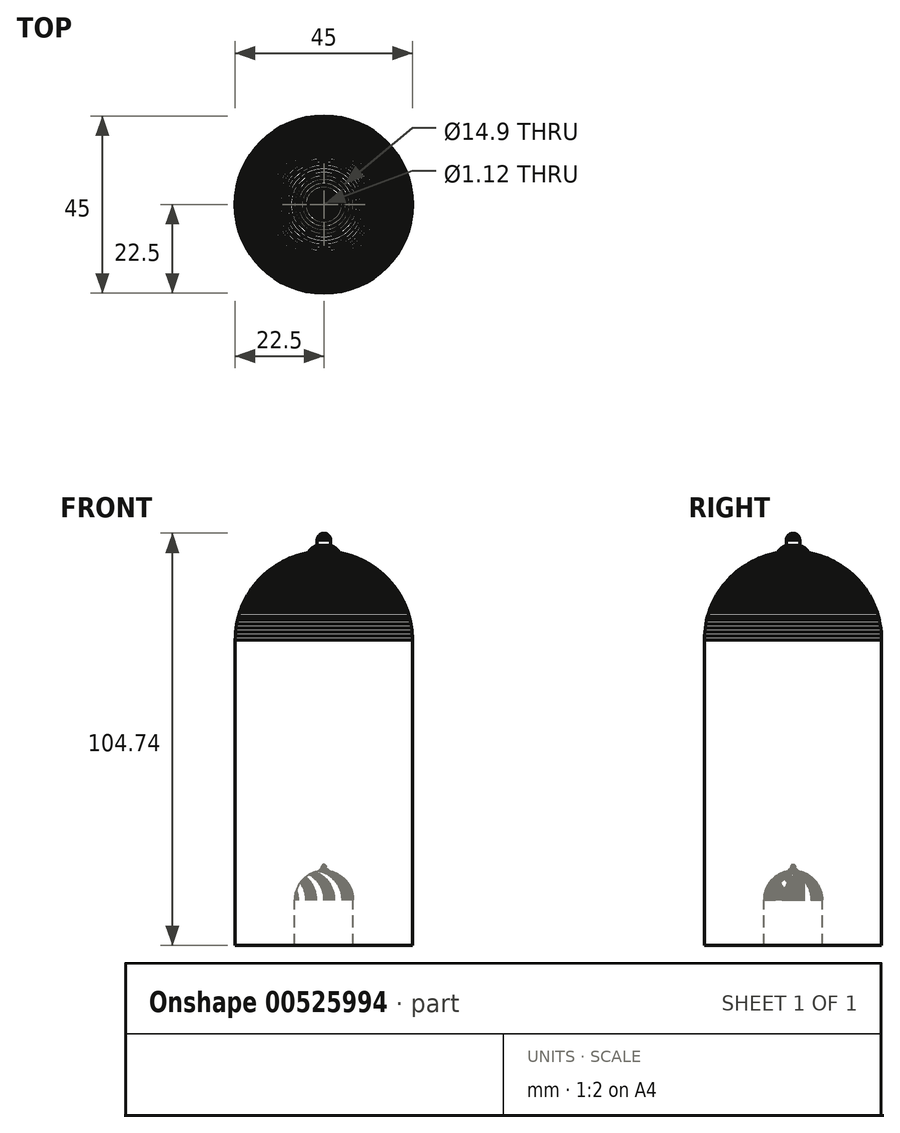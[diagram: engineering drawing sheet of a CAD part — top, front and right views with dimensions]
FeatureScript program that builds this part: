
annotation { "Feature Type Name" : "Feature", "Feature Type Description" : "" }
export const myFeature = defineFeature(function(context is Context, id is Id, definition is map)
    precondition{}
    {
        {
            var Q0;
            Q0=qCreatedBy(makeId("Front.planeOp"),FACE);
            var sketch = newSketch(context, id + "F0", { "sketchPlane" : qUnion([Q0])});
            skLineSegment(sketch, "E0", {"start": v(3.98, 47.42) * mm, "end": v(3.94, 47.5) * mm});
            skLineSegment(sketch, "E1", {"start": v(3.94, 47.5) * mm, "end": v(3.9, 47.57) * mm});
            skLineSegment(sketch, "E2", {"start": v(3.9, 47.57) * mm, "end": v(3.86, 47.65) * mm});
            skLineSegment(sketch, "E3", {"start": v(3.86, 47.65) * mm, "end": v(3.82, 47.72) * mm});
            skLineSegment(sketch, "E4", {"start": v(3.82, 47.72) * mm, "end": v(3.77, 47.8) * mm});
            skLineSegment(sketch, "E5", {"start": v(3.77, 47.8) * mm, "end": v(3.73, 47.87) * mm});
            skLineSegment(sketch, "E6", {"start": v(3.73, 47.87) * mm, "end": v(3.67, 47.94) * mm});
            skLineSegment(sketch, "E7", {"start": v(3.67, 47.94) * mm, "end": v(3.62, 48.01) * mm});
            skLineSegment(sketch, "E8", {"start": v(3.62, 48.01) * mm, "end": v(3.57, 48.08) * mm});
            skLineSegment(sketch, "E9", {"start": v(3.57, 48.08) * mm, "end": v(3.5, 48.15) * mm});
            skLineSegment(sketch, "E10", {"start": v(3.5, 48.15) * mm, "end": v(3.45, 48.22) * mm});
            skLineSegment(sketch, "E11", {"start": v(3.45, 48.22) * mm, "end": v(3.38, 48.28) * mm});
            skLineSegment(sketch, "E12", {"start": v(3.38, 48.28) * mm, "end": v(3.32, 48.34) * mm});
            skLineSegment(sketch, "E13", {"start": v(3.32, 48.34) * mm, "end": v(3.25, 48.4) * mm});
            skLineSegment(sketch, "E14", {"start": v(3.25, 48.4) * mm, "end": v(3.18, 48.47) * mm});
            skLineSegment(sketch, "E15", {"start": v(3.18, 48.47) * mm, "end": v(3.1, 48.53) * mm});
            skLineSegment(sketch, "E16", {"start": v(3.1, 48.53) * mm, "end": v(3.03, 48.59) * mm});
            skLineSegment(sketch, "E17", {"start": v(3.03, 48.59) * mm, "end": v(2.96, 48.65) * mm});
            skLineSegment(sketch, "E18", {"start": v(2.96, 48.65) * mm, "end": v(2.88, 48.7) * mm});
            skLineSegment(sketch, "E19", {"start": v(2.88, 48.7) * mm, "end": v(2.8, 48.76) * mm});
            skLineSegment(sketch, "E20", {"start": v(2.8, 48.76) * mm, "end": v(2.72, 48.8) * mm});
            skLineSegment(sketch, "E21", {"start": v(2.72, 48.8) * mm, "end": v(2.63, 48.86) * mm});
            skLineSegment(sketch, "E22", {"start": v(2.63, 48.86) * mm, "end": v(2.55, 48.9) * mm});
            skLineSegment(sketch, "E23", {"start": v(2.55, 48.9) * mm, "end": v(2.46, 48.96) * mm});
            skLineSegment(sketch, "E24", {"start": v(2.46, 48.96) * mm, "end": v(2.37, 49) * mm});
            skLineSegment(sketch, "E25", {"start": v(2.37, 49) * mm, "end": v(2.28, 49.05) * mm});
            skLineSegment(sketch, "E26", {"start": v(2.28, 49.05) * mm, "end": v(2.19, 49.1) * mm});
            skLineSegment(sketch, "E27", {"start": v(2.19, 49.1) * mm, "end": v(2.1, 49.13) * mm});
            skLineSegment(sketch, "E28", {"start": v(2.1, 49.13) * mm, "end": v(2, 49.17) * mm});
            skLineSegment(sketch, "E29", {"start": v(2, 49.17) * mm, "end": v(1.9, 49.2) * mm});
            skLineSegment(sketch, "E30", {"start": v(1.9, 49.2) * mm, "end": v(1.8, 49.25) * mm});
            skLineSegment(sketch, "E31", {"start": v(1.8, 49.25) * mm, "end": v(1.7, 49.28) * mm});
            skLineSegment(sketch, "E32", {"start": v(1.7, 49.28) * mm, "end": v(1.7, 49.32) * mm});
            skLineSegment(sketch, "E33", {"start": v(1.7, 49.32) * mm, "end": v(1.7, 49.37) * mm});
            skLineSegment(sketch, "E34", {"start": v(1.7, 49.37) * mm, "end": v(1.7, 49.4) * mm});
            skLineSegment(sketch, "E35", {"start": v(1.7, 49.4) * mm, "end": v(1.7, 49.45) * mm});
            skLineSegment(sketch, "E36", {"start": v(1.7, 49.45) * mm, "end": v(1.7, 49.5) * mm});
            skLineSegment(sketch, "E37", {"start": v(1.7, 49.5) * mm, "end": v(1.7, 49.54) * mm});
            skLineSegment(sketch, "E38", {"start": v(1.7, 49.54) * mm, "end": v(1.7, 49.58) * mm});
            skLineSegment(sketch, "E39", {"start": v(1.7, 49.58) * mm, "end": v(1.7, 49.63) * mm});
            skLineSegment(sketch, "E40", {"start": v(1.7, 49.63) * mm, "end": v(1.7, 49.67) * mm});
            skLineSegment(sketch, "E41", {"start": v(1.7, 49.67) * mm, "end": v(1.7, 49.71) * mm});
            skLineSegment(sketch, "E42", {"start": v(1.7, 49.71) * mm, "end": v(1.7, 49.76) * mm});
            skLineSegment(sketch, "E43", {"start": v(1.7, 49.76) * mm, "end": v(1.7, 49.8) * mm});
            skLineSegment(sketch, "E44", {"start": v(1.7, 49.8) * mm, "end": v(1.7, 49.84) * mm});
            skLineSegment(sketch, "E45", {"start": v(1.7, 49.84) * mm, "end": v(1.7, 49.89) * mm});
            skLineSegment(sketch, "E46", {"start": v(1.7, 49.89) * mm, "end": v(1.7, 49.93) * mm});
            skLineSegment(sketch, "E47", {"start": v(1.7, 49.93) * mm, "end": v(1.7, 49.97) * mm});
            skLineSegment(sketch, "E48", {"start": v(1.7, 49.97) * mm, "end": v(1.7, 50.02) * mm});
            skLineSegment(sketch, "E49", {"start": v(1.7, 50.02) * mm, "end": v(1.7, 50.06) * mm});
            skLineSegment(sketch, "E50", {"start": v(1.7, 50.06) * mm, "end": v(1.7, 50.1) * mm});
            skLineSegment(sketch, "E51", {"start": v(1.7, 50.1) * mm, "end": v(1.7, 50.15) * mm});
            skLineSegment(sketch, "E52", {"start": v(1.7, 50.15) * mm, "end": v(1.7, 50.2) * mm});
            skLineSegment(sketch, "E53", {"start": v(1.7, 50.2) * mm, "end": v(1.7, 50.23) * mm});
            skLineSegment(sketch, "E54", {"start": v(1.7, 50.23) * mm, "end": v(1.7, 50.28) * mm});
            skLineSegment(sketch, "E55", {"start": v(1.7, 50.28) * mm, "end": v(1.7, 50.32) * mm});
            skLineSegment(sketch, "E56", {"start": v(1.7, 50.32) * mm, "end": v(1.7, 50.36) * mm});
            skLineSegment(sketch, "E57", {"start": v(1.7, 50.36) * mm, "end": v(1.7, 50.4) * mm});
            skLineSegment(sketch, "E58", {"start": v(1.7, 50.4) * mm, "end": v(1.7, 50.45) * mm});
            skLineSegment(sketch, "E59", {"start": v(1.7, 50.45) * mm, "end": v(1.7, 50.5) * mm});
            skLineSegment(sketch, "E60", {"start": v(1.7, 50.5) * mm, "end": v(1.7, 50.54) * mm});
            skLineSegment(sketch, "E61", {"start": v(1.7, 50.54) * mm, "end": v(1.7, 50.58) * mm});
            skLineSegment(sketch, "E62", {"start": v(1.7, 50.58) * mm, "end": v(1.7, 50.63) * mm});
            skLineSegment(sketch, "E63", {"start": v(1.7, 50.63) * mm, "end": v(1.7, 50.67) * mm});
            skLineSegment(sketch, "E64", {"start": v(1.7, 50.67) * mm, "end": v(1.7, 50.76) * mm});
            skLineSegment(sketch, "E65", {"start": v(1.7, 50.76) * mm, "end": v(1.69, 50.84) * mm});
            skLineSegment(sketch, "E66", {"start": v(1.69, 50.84) * mm, "end": v(1.68, 50.93) * mm});
            skLineSegment(sketch, "E67", {"start": v(1.68, 50.93) * mm, "end": v(1.66, 51.01) * mm});
            skLineSegment(sketch, "E68", {"start": v(1.66, 51.01) * mm, "end": v(1.64, 51.1) * mm});
            skLineSegment(sketch, "E69", {"start": v(1.64, 51.1) * mm, "end": v(1.62, 51.17) * mm});
            skLineSegment(sketch, "E70", {"start": v(1.62, 51.17) * mm, "end": v(1.6, 51.25) * mm});
            skLineSegment(sketch, "E71", {"start": v(1.6, 51.25) * mm, "end": v(1.56, 51.33) * mm});
            skLineSegment(sketch, "E72", {"start": v(1.56, 51.33) * mm, "end": v(1.53, 51.4) * mm});
            skLineSegment(sketch, "E73", {"start": v(1.53, 51.4) * mm, "end": v(1.5, 51.48) * mm});
            skLineSegment(sketch, "E74", {"start": v(1.5, 51.48) * mm, "end": v(1.45, 51.55) * mm});
            skLineSegment(sketch, "E75", {"start": v(1.45, 51.55) * mm, "end": v(1.4, 51.62) * mm});
            skLineSegment(sketch, "E76", {"start": v(1.4, 51.62) * mm, "end": v(1.36, 51.68) * mm});
            skLineSegment(sketch, "E77", {"start": v(1.36, 51.68) * mm, "end": v(1.3, 51.75) * mm});
            skLineSegment(sketch, "E78", {"start": v(1.3, 51.75) * mm, "end": v(1.26, 51.8) * mm});
            skLineSegment(sketch, "E79", {"start": v(1.26, 51.8) * mm, "end": v(1.2, 51.87) * mm});
            skLineSegment(sketch, "E80", {"start": v(1.2, 51.87) * mm, "end": v(1.14, 51.92) * mm});
            skLineSegment(sketch, "E81", {"start": v(1.14, 51.92) * mm, "end": v(1.08, 51.98) * mm});
            skLineSegment(sketch, "E82", {"start": v(1.08, 51.98) * mm, "end": v(1.02, 52.03) * mm});
            skLineSegment(sketch, "E83", {"start": v(1.02, 52.03) * mm, "end": v(0.95, 52.08) * mm});
            skLineSegment(sketch, "E84", {"start": v(0.95, 52.08) * mm, "end": v(0.88, 52.12) * mm});
            skLineSegment(sketch, "E85", {"start": v(0.88, 52.12) * mm, "end": v(0.8, 52.16) * mm});
            skLineSegment(sketch, "E86", {"start": v(0.8, 52.16) * mm, "end": v(0.74, 52.2) * mm});
            skLineSegment(sketch, "E87", {"start": v(0.74, 52.2) * mm, "end": v(0.66, 52.23) * mm});
            skLineSegment(sketch, "E88", {"start": v(0.66, 52.23) * mm, "end": v(0.58, 52.26) * mm});
            skLineSegment(sketch, "E89", {"start": v(0.58, 52.26) * mm, "end": v(0.5, 52.29) * mm});
            skLineSegment(sketch, "E90", {"start": v(0.5, 52.29) * mm, "end": v(0.42, 52.31) * mm});
            skLineSegment(sketch, "E91", {"start": v(0.42, 52.31) * mm, "end": v(0.34, 52.33) * mm});
            skLineSegment(sketch, "E92", {"start": v(0.34, 52.33) * mm, "end": v(0.26, 52.35) * mm});
            skLineSegment(sketch, "E93", {"start": v(0.26, 52.35) * mm, "end": v(0.17, 52.36) * mm});
            skLineSegment(sketch, "E94", {"start": v(0.17, 52.36) * mm, "end": v(0.09, 52.36) * mm});
            skLineSegment(sketch, "E95", {"start": v(0, 52.37) * mm, "end": v(-0.09, 52.36) * mm});
            skLineSegment(sketch, "E96", {"start": v(-0.09, 52.36) * mm, "end": v(-0.17, 52.36) * mm});
            skLineSegment(sketch, "E97", {"start": v(-0.17, 52.36) * mm, "end": v(-0.26, 52.35) * mm});
            skLineSegment(sketch, "E98", {"start": v(-0.26, 52.35) * mm, "end": v(-0.34, 52.33) * mm});
            skLineSegment(sketch, "E99", {"start": v(-0.34, 52.33) * mm, "end": v(-0.42, 52.31) * mm});
            skLineSegment(sketch, "E100", {"start": v(-0.42, 52.31) * mm, "end": v(-0.5, 52.29) * mm});
            skLineSegment(sketch, "E101", {"start": v(-0.5, 52.29) * mm, "end": v(-0.58, 52.26) * mm});
            skLineSegment(sketch, "E102", {"start": v(-0.58, 52.26) * mm, "end": v(-0.66, 52.23) * mm});
            skLineSegment(sketch, "E103", {"start": v(-0.66, 52.23) * mm, "end": v(-0.74, 52.2) * mm});
            skLineSegment(sketch, "E104", {"start": v(-0.74, 52.2) * mm, "end": v(-0.8, 52.16) * mm});
            skLineSegment(sketch, "E105", {"start": v(-0.8, 52.16) * mm, "end": v(-0.88, 52.12) * mm});
            skLineSegment(sketch, "E106", {"start": v(-0.88, 52.12) * mm, "end": v(-0.95, 52.08) * mm});
            skLineSegment(sketch, "E107", {"start": v(-0.95, 52.08) * mm, "end": v(-1.01, 52.03) * mm});
            skLineSegment(sketch, "E108", {"start": v(-1.01, 52.03) * mm, "end": v(-1.08, 51.98) * mm});
            skLineSegment(sketch, "E109", {"start": v(-1.08, 51.98) * mm, "end": v(-1.14, 51.92) * mm});
            skLineSegment(sketch, "E110", {"start": v(-1.14, 51.92) * mm, "end": v(-1.2, 51.87) * mm});
            skLineSegment(sketch, "E111", {"start": v(-1.2, 51.87) * mm, "end": v(-1.26, 51.8) * mm});
            skLineSegment(sketch, "E112", {"start": v(-1.26, 51.8) * mm, "end": v(-1.3, 51.75) * mm});
            skLineSegment(sketch, "E113", {"start": v(-1.3, 51.75) * mm, "end": v(-1.36, 51.68) * mm});
            skLineSegment(sketch, "E114", {"start": v(-1.36, 51.68) * mm, "end": v(-1.4, 51.62) * mm});
            skLineSegment(sketch, "E115", {"start": v(-1.4, 51.62) * mm, "end": v(-1.45, 51.55) * mm});
            skLineSegment(sketch, "E116", {"start": v(-1.45, 51.55) * mm, "end": v(-1.5, 51.48) * mm});
            skLineSegment(sketch, "E117", {"start": v(-1.5, 51.48) * mm, "end": v(-1.53, 51.4) * mm});
            skLineSegment(sketch, "E118", {"start": v(-1.53, 51.4) * mm, "end": v(-1.56, 51.33) * mm});
            skLineSegment(sketch, "E119", {"start": v(-1.56, 51.33) * mm, "end": v(-1.6, 51.25) * mm});
            skLineSegment(sketch, "E120", {"start": v(-1.6, 51.25) * mm, "end": v(-1.62, 51.17) * mm});
            skLineSegment(sketch, "E121", {"start": v(-1.62, 51.17) * mm, "end": v(-1.64, 51.1) * mm});
            skLineSegment(sketch, "E122", {"start": v(-1.64, 51.1) * mm, "end": v(-1.66, 51.01) * mm});
            skLineSegment(sketch, "E123", {"start": v(-1.66, 51.01) * mm, "end": v(-1.68, 50.93) * mm});
            skLineSegment(sketch, "E124", {"start": v(-1.68, 50.93) * mm, "end": v(-1.69, 50.84) * mm});
            skLineSegment(sketch, "E125", {"start": v(-1.69, 50.84) * mm, "end": v(-1.7, 50.76) * mm});
            skLineSegment(sketch, "E126", {"start": v(-1.7, 50.76) * mm, "end": v(-1.7, 50.67) * mm});
            skLineSegment(sketch, "E127", {"start": v(-1.7, 50.67) * mm, "end": v(-1.7, 50.63) * mm});
            skLineSegment(sketch, "E128", {"start": v(-1.7, 50.63) * mm, "end": v(-1.7, 50.58) * mm});
            skLineSegment(sketch, "E129", {"start": v(-1.7, 50.58) * mm, "end": v(-1.7, 50.54) * mm});
            skLineSegment(sketch, "E130", {"start": v(-1.7, 50.54) * mm, "end": v(-1.7, 50.5) * mm});
            skLineSegment(sketch, "E131", {"start": v(-1.7, 50.5) * mm, "end": v(-1.7, 50.45) * mm});
            skLineSegment(sketch, "E132", {"start": v(-1.7, 50.45) * mm, "end": v(-1.7, 50.4) * mm});
            skLineSegment(sketch, "E133", {"start": v(-1.7, 50.4) * mm, "end": v(-1.7, 50.36) * mm});
            skLineSegment(sketch, "E134", {"start": v(-1.7, 50.36) * mm, "end": v(-1.7, 50.32) * mm});
            skLineSegment(sketch, "E135", {"start": v(-1.7, 50.32) * mm, "end": v(-1.7, 50.28) * mm});
            skLineSegment(sketch, "E136", {"start": v(-1.7, 50.28) * mm, "end": v(-1.7, 50.23) * mm});
            skLineSegment(sketch, "E137", {"start": v(-1.7, 50.23) * mm, "end": v(-1.7, 50.2) * mm});
            skLineSegment(sketch, "E138", {"start": v(-1.7, 50.2) * mm, "end": v(-1.7, 50.15) * mm});
            skLineSegment(sketch, "E139", {"start": v(-1.7, 50.15) * mm, "end": v(-1.7, 50.1) * mm});
            skLineSegment(sketch, "E140", {"start": v(-1.7, 50.1) * mm, "end": v(-1.7, 50.06) * mm});
            skLineSegment(sketch, "E141", {"start": v(-1.7, 50.06) * mm, "end": v(-1.7, 50.02) * mm});
            skLineSegment(sketch, "E142", {"start": v(-1.7, 50.02) * mm, "end": v(-1.7, 49.97) * mm});
            skLineSegment(sketch, "E143", {"start": v(-1.7, 49.97) * mm, "end": v(-1.7, 49.93) * mm});
            skLineSegment(sketch, "E144", {"start": v(-1.7, 49.93) * mm, "end": v(-1.7, 49.89) * mm});
            skLineSegment(sketch, "E145", {"start": v(-1.7, 49.89) * mm, "end": v(-1.7, 49.84) * mm});
            skLineSegment(sketch, "E146", {"start": v(-1.7, 49.84) * mm, "end": v(-1.7, 49.8) * mm});
            skLineSegment(sketch, "E147", {"start": v(-1.7, 49.8) * mm, "end": v(-1.7, 49.76) * mm});
            skLineSegment(sketch, "E148", {"start": v(-1.7, 49.76) * mm, "end": v(-1.7, 49.71) * mm});
            skLineSegment(sketch, "E149", {"start": v(-1.7, 49.71) * mm, "end": v(-1.7, 49.67) * mm});
            skLineSegment(sketch, "E150", {"start": v(-1.7, 49.67) * mm, "end": v(-1.7, 49.63) * mm});
            skLineSegment(sketch, "E151", {"start": v(-1.7, 49.63) * mm, "end": v(-1.7, 49.58) * mm});
            skLineSegment(sketch, "E152", {"start": v(-1.7, 49.58) * mm, "end": v(-1.7, 49.54) * mm});
            skLineSegment(sketch, "E153", {"start": v(-1.7, 49.54) * mm, "end": v(-1.7, 49.5) * mm});
            skLineSegment(sketch, "E154", {"start": v(-1.7, 49.5) * mm, "end": v(-1.7, 49.45) * mm});
            skLineSegment(sketch, "E155", {"start": v(-1.7, 49.45) * mm, "end": v(-1.7, 49.4) * mm});
            skLineSegment(sketch, "E156", {"start": v(-1.7, 49.4) * mm, "end": v(-1.7, 49.37) * mm});
            skLineSegment(sketch, "E157", {"start": v(-1.7, 49.37) * mm, "end": v(-1.7, 49.32) * mm});
            skLineSegment(sketch, "E158", {"start": v(-1.7, 49.32) * mm, "end": v(-1.7, 49.28) * mm});
            skLineSegment(sketch, "E159", {"start": v(-1.7, 49.28) * mm, "end": v(-1.8, 49.25) * mm});
            skLineSegment(sketch, "E160", {"start": v(-1.8, 49.25) * mm, "end": v(-1.9, 49.2) * mm});
            skLineSegment(sketch, "E161", {"start": v(-1.9, 49.2) * mm, "end": v(-2, 49.17) * mm});
            skLineSegment(sketch, "E162", {"start": v(-2, 49.17) * mm, "end": v(-2.1, 49.13) * mm});
            skLineSegment(sketch, "E163", {"start": v(-2.1, 49.13) * mm, "end": v(-2.19, 49.1) * mm});
            skLineSegment(sketch, "E164", {"start": v(-2.19, 49.1) * mm, "end": v(-2.28, 49.05) * mm});
            skLineSegment(sketch, "E165", {"start": v(-2.28, 49.05) * mm, "end": v(-2.37, 49) * mm});
            skLineSegment(sketch, "E166", {"start": v(-2.37, 49) * mm, "end": v(-2.46, 48.96) * mm});
            skLineSegment(sketch, "E167", {"start": v(-2.46, 48.96) * mm, "end": v(-2.55, 48.9) * mm});
            skLineSegment(sketch, "E168", {"start": v(-2.55, 48.9) * mm, "end": v(-2.63, 48.86) * mm});
            skLineSegment(sketch, "E169", {"start": v(-2.63, 48.86) * mm, "end": v(-2.72, 48.8) * mm});
            skLineSegment(sketch, "E170", {"start": v(-2.72, 48.8) * mm, "end": v(-2.8, 48.76) * mm});
            skLineSegment(sketch, "E171", {"start": v(-2.8, 48.76) * mm, "end": v(-2.88, 48.7) * mm});
            skLineSegment(sketch, "E172", {"start": v(-2.88, 48.7) * mm, "end": v(-2.96, 48.65) * mm});
            skLineSegment(sketch, "E173", {"start": v(-2.96, 48.65) * mm, "end": v(-3.03, 48.59) * mm});
            skLineSegment(sketch, "E174", {"start": v(-3.03, 48.59) * mm, "end": v(-3.1, 48.53) * mm});
            skLineSegment(sketch, "E175", {"start": v(-3.1, 48.53) * mm, "end": v(-3.18, 48.47) * mm});
            skLineSegment(sketch, "E176", {"start": v(-3.18, 48.47) * mm, "end": v(-3.25, 48.4) * mm});
            skLineSegment(sketch, "E177", {"start": v(-3.25, 48.4) * mm, "end": v(-3.32, 48.34) * mm});
            skLineSegment(sketch, "E178", {"start": v(-3.32, 48.34) * mm, "end": v(-3.38, 48.28) * mm});
            skLineSegment(sketch, "E179", {"start": v(-3.38, 48.28) * mm, "end": v(-3.45, 48.22) * mm});
            skLineSegment(sketch, "E180", {"start": v(-3.45, 48.22) * mm, "end": v(-3.5, 48.15) * mm});
            skLineSegment(sketch, "E181", {"start": v(-3.5, 48.15) * mm, "end": v(-3.57, 48.08) * mm});
            skLineSegment(sketch, "E182", {"start": v(-3.57, 48.08) * mm, "end": v(-3.62, 48.01) * mm});
            skLineSegment(sketch, "E183", {"start": v(-3.62, 48.01) * mm, "end": v(-3.67, 47.94) * mm});
            skLineSegment(sketch, "E184", {"start": v(-3.67, 47.94) * mm, "end": v(-3.73, 47.87) * mm});
            skLineSegment(sketch, "E185", {"start": v(-3.73, 47.87) * mm, "end": v(-3.77, 47.8) * mm});
            skLineSegment(sketch, "E186", {"start": v(-3.77, 47.8) * mm, "end": v(-3.82, 47.72) * mm});
            skLineSegment(sketch, "E187", {"start": v(-3.82, 47.72) * mm, "end": v(-3.86, 47.65) * mm});
            skLineSegment(sketch, "E188", {"start": v(-3.86, 47.65) * mm, "end": v(-3.9, 47.57) * mm});
            skLineSegment(sketch, "E189", {"start": v(-3.9, 47.57) * mm, "end": v(-3.94, 47.5) * mm});
            skLineSegment(sketch, "E190", {"start": v(-3.94, 47.5) * mm, "end": v(-3.98, 47.42) * mm});
            skLineSegment(sketch, "E191", {"start": v(-3.98, 47.42) * mm, "end": v(-4.95, 47.22) * mm});
            skLineSegment(sketch, "E192", {"start": v(-4.95, 47.22) * mm, "end": v(-5.92, 46.98) * mm});
            skLineSegment(sketch, "E193", {"start": v(-5.92, 46.98) * mm, "end": v(-6.87, 46.7) * mm});
            skLineSegment(sketch, "E194", {"start": v(-6.87, 46.7) * mm, "end": v(-7.8, 46.38) * mm});
            skLineSegment(sketch, "E195", {"start": v(-7.8, 46.38) * mm, "end": v(-8.7, 46.02) * mm});
            skLineSegment(sketch, "E196", {"start": v(-8.7, 46.02) * mm, "end": v(-9.6, 45.63) * mm});
            skLineSegment(sketch, "E197", {"start": v(-9.6, 45.63) * mm, "end": v(-10.46, 45.2) * mm});
            skLineSegment(sketch, "E198", {"start": v(-10.46, 45.2) * mm, "end": v(-11.31, 44.72) * mm});
            skLineSegment(sketch, "E199", {"start": v(-11.31, 44.72) * mm, "end": v(-12.14, 44.22) * mm});
            skLineSegment(sketch, "E200", {"start": v(-12.14, 44.22) * mm, "end": v(-12.94, 43.68) * mm});
            skLineSegment(sketch, "E201", {"start": v(-12.94, 43.68) * mm, "end": v(-13.71, 43.1) * mm});
            skLineSegment(sketch, "E202", {"start": v(-13.71, 43.1) * mm, "end": v(-14.46, 42.5) * mm});
            skLineSegment(sketch, "E203", {"start": v(-14.46, 42.5) * mm, "end": v(-15.19, 41.87) * mm});
            skLineSegment(sketch, "E204", {"start": v(-15.19, 41.87) * mm, "end": v(-15.88, 41.2) * mm});
            skLineSegment(sketch, "E205", {"start": v(-15.88, 41.2) * mm, "end": v(-16.55, 40.52) * mm});
            skLineSegment(sketch, "E206", {"start": v(-16.55, 40.52) * mm, "end": v(-17.19, 39.8) * mm});
            skLineSegment(sketch, "E207", {"start": v(-17.19, 39.8) * mm, "end": v(-17.8, 39.05) * mm});
            skLineSegment(sketch, "E208", {"start": v(-17.8, 39.05) * mm, "end": v(-18.37, 38.27) * mm});
            skLineSegment(sketch, "E209", {"start": v(-18.37, 38.27) * mm, "end": v(-18.9, 37.47) * mm});
            skLineSegment(sketch, "E210", {"start": v(-18.9, 37.47) * mm, "end": v(-19.42, 36.65) * mm});
            skLineSegment(sketch, "E211", {"start": v(-19.42, 36.65) * mm, "end": v(-19.89, 35.8) * mm});
            skLineSegment(sketch, "E212", {"start": v(-19.89, 35.8) * mm, "end": v(-20.32, 34.94) * mm});
            skLineSegment(sketch, "E213", {"start": v(-20.32, 34.94) * mm, "end": v(-20.72, 34.05) * mm});
            skLineSegment(sketch, "E214", {"start": v(-20.72, 34.05) * mm, "end": v(-21.09, 33.14) * mm});
            skLineSegment(sketch, "E215", {"start": v(-21.09, 33.14) * mm, "end": v(-21.4, 32.21) * mm});
            skLineSegment(sketch, "E216", {"start": v(-21.4, 32.21) * mm, "end": v(-21.7, 31.27) * mm});
            skLineSegment(sketch, "E217", {"start": v(-21.7, 31.27) * mm, "end": v(-21.94, 30.3) * mm});
            skLineSegment(sketch, "E218", {"start": v(-21.94, 30.3) * mm, "end": v(-22.14, 29.33) * mm});
            skLineSegment(sketch, "E219", {"start": v(-22.14, 29.33) * mm, "end": v(-22.3, 28.34) * mm});
            skLineSegment(sketch, "E220", {"start": v(-22.3, 28.34) * mm, "end": v(-22.4, 27.33) * mm});
            skLineSegment(sketch, "E221", {"start": v(-22.4, 27.33) * mm, "end": v(-22.48, 26.3) * mm});
            skLineSegment(sketch, "E222", {"start": v(-22.48, 26.3) * mm, "end": v(-22.5, 25.28) * mm});
            skLineSegment(sketch, "E223", {"start": v(-22.5, 25.28) * mm, "end": v(-22.5, 22.85) * mm});
            skLineSegment(sketch, "E224", {"start": v(-22.5, 22.85) * mm, "end": v(-22.5, 20.42) * mm});
            skLineSegment(sketch, "E225", {"start": v(-22.5, 20.42) * mm, "end": v(-22.5, 18) * mm});
            skLineSegment(sketch, "E226", {"start": v(-22.5, 18) * mm, "end": v(-22.5, 15.57) * mm});
            skLineSegment(sketch, "E227", {"start": v(-22.5, 15.57) * mm, "end": v(-22.5, 13.14) * mm});
            skLineSegment(sketch, "E228", {"start": v(-22.5, 13.14) * mm, "end": v(-22.5, 10.72) * mm});
            skLineSegment(sketch, "E229", {"start": v(-22.5, 10.72) * mm, "end": v(-22.5, 8.3) * mm});
            skLineSegment(sketch, "E230", {"start": v(-22.5, 8.3) * mm, "end": v(-22.5, 5.87) * mm});
            skLineSegment(sketch, "E231", {"start": v(-22.5, 5.87) * mm, "end": v(-22.5, 3.44) * mm});
            skLineSegment(sketch, "E232", {"start": v(-22.5, 3.44) * mm, "end": v(-22.5, 1.01) * mm});
            skLineSegment(sketch, "E233", {"start": v(-22.5, 1.01) * mm, "end": v(-22.5, -1.41) * mm});
            skLineSegment(sketch, "E234", {"start": v(-22.5, -1.41) * mm, "end": v(-22.5, -3.84) * mm});
            skLineSegment(sketch, "E235", {"start": v(-22.5, -3.84) * mm, "end": v(-22.5, -6.27) * mm});
            skLineSegment(sketch, "E236", {"start": v(-22.5, -6.27) * mm, "end": v(-22.5, -8.7) * mm});
            skLineSegment(sketch, "E237", {"start": v(-22.5, -8.7) * mm, "end": v(-22.5, -11.12) * mm});
            skLineSegment(sketch, "E238", {"start": v(-22.5, -11.12) * mm, "end": v(-22.5, -13.54) * mm});
            skLineSegment(sketch, "E239", {"start": v(-22.5, -13.54) * mm, "end": v(-22.5, -15.97) * mm});
            skLineSegment(sketch, "E240", {"start": v(-22.5, -15.97) * mm, "end": v(-22.5, -18.4) * mm});
            skLineSegment(sketch, "E241", {"start": v(-22.5, -18.4) * mm, "end": v(-22.5, -20.82) * mm});
            skLineSegment(sketch, "E242", {"start": v(-22.5, -20.82) * mm, "end": v(-22.5, -23.25) * mm});
            skLineSegment(sketch, "E243", {"start": v(-22.5, -23.25) * mm, "end": v(-22.5, -25.68) * mm});
            skLineSegment(sketch, "E244", {"start": v(-22.5, -25.68) * mm, "end": v(-22.5, -28.1) * mm});
            skLineSegment(sketch, "E245", {"start": v(-22.5, -28.1) * mm, "end": v(-22.5, -30.53) * mm});
            skLineSegment(sketch, "E246", {"start": v(-22.5, -30.53) * mm, "end": v(-22.5, -32.96) * mm});
            skLineSegment(sketch, "E247", {"start": v(-22.5, -32.96) * mm, "end": v(-22.5, -35.38) * mm});
            skLineSegment(sketch, "E248", {"start": v(-22.5, -35.38) * mm, "end": v(-22.5, -37.8) * mm});
            skLineSegment(sketch, "E249", {"start": v(-22.5, -37.8) * mm, "end": v(-22.5, -40.23) * mm});
            skLineSegment(sketch, "E250", {"start": v(-22.5, -40.23) * mm, "end": v(-22.5, -42.66) * mm});
            skLineSegment(sketch, "E251", {"start": v(-22.5, -42.66) * mm, "end": v(-22.5, -45.09) * mm});
            skLineSegment(sketch, "E252", {"start": v(-22.5, -45.09) * mm, "end": v(-22.5, -47.51) * mm});
            skLineSegment(sketch, "E253", {"start": v(-22.5, -47.51) * mm, "end": v(-22.5, -49.94) * mm});
            skLineSegment(sketch, "E254", {"start": v(-22.5, -49.94) * mm, "end": v(-22.5, -52.37) * mm});
            skLineSegment(sketch, "E255", {"start": v(-22.5, -52.37) * mm, "end": v(-22.03, -52.37) * mm});
            skLineSegment(sketch, "E256", {"start": v(-22.03, -52.37) * mm, "end": v(-21.56, -52.37) * mm});
            skLineSegment(sketch, "E257", {"start": v(-21.56, -52.37) * mm, "end": v(-21.09, -52.37) * mm});
            skLineSegment(sketch, "E258", {"start": v(-21.09, -52.37) * mm, "end": v(-20.62, -52.37) * mm});
            skLineSegment(sketch, "E259", {"start": v(-20.62, -52.37) * mm, "end": v(-20.15, -52.37) * mm});
            skLineSegment(sketch, "E260", {"start": v(-20.15, -52.37) * mm, "end": v(-19.68, -52.37) * mm});
            skLineSegment(sketch, "E261", {"start": v(-19.68, -52.37) * mm, "end": v(-19.2, -52.37) * mm});
            skLineSegment(sketch, "E262", {"start": v(-19.2, -52.37) * mm, "end": v(-18.74, -52.37) * mm});
            skLineSegment(sketch, "E263", {"start": v(-18.74, -52.37) * mm, "end": v(-18.27, -52.37) * mm});
            skLineSegment(sketch, "E264", {"start": v(-18.27, -52.37) * mm, "end": v(-17.8, -52.37) * mm});
            skLineSegment(sketch, "E265", {"start": v(-17.8, -52.37) * mm, "end": v(-17.33, -52.37) * mm});
            skLineSegment(sketch, "E266", {"start": v(-17.33, -52.37) * mm, "end": v(-16.86, -52.37) * mm});
            skLineSegment(sketch, "E267", {"start": v(-16.86, -52.37) * mm, "end": v(-16.39, -52.37) * mm});
            skLineSegment(sketch, "E268", {"start": v(-16.39, -52.37) * mm, "end": v(-15.91, -52.37) * mm});
            skLineSegment(sketch, "E269", {"start": v(-15.91, -52.37) * mm, "end": v(-15.44, -52.37) * mm});
            skLineSegment(sketch, "E270", {"start": v(-15.44, -52.37) * mm, "end": v(-14.97, -52.37) * mm});
            skLineSegment(sketch, "E271", {"start": v(-14.97, -52.37) * mm, "end": v(-14.5, -52.37) * mm});
            skLineSegment(sketch, "E272", {"start": v(-14.5, -52.37) * mm, "end": v(-14.03, -52.37) * mm});
            skLineSegment(sketch, "E273", {"start": v(-14.03, -52.37) * mm, "end": v(-13.56, -52.37) * mm});
            skLineSegment(sketch, "E274", {"start": v(-13.56, -52.37) * mm, "end": v(-13.1, -52.37) * mm});
            skLineSegment(sketch, "E275", {"start": v(-13.1, -52.37) * mm, "end": v(-12.62, -52.37) * mm});
            skLineSegment(sketch, "E276", {"start": v(-12.62, -52.37) * mm, "end": v(-12.15, -52.37) * mm});
            skLineSegment(sketch, "E277", {"start": v(-12.15, -52.37) * mm, "end": v(-11.68, -52.37) * mm});
            skLineSegment(sketch, "E278", {"start": v(-11.68, -52.37) * mm, "end": v(-11.21, -52.37) * mm});
            skLineSegment(sketch, "E279", {"start": v(-11.21, -52.37) * mm, "end": v(-10.74, -52.37) * mm});
            skLineSegment(sketch, "E280", {"start": v(-10.74, -52.37) * mm, "end": v(-10.27, -52.37) * mm});
            skLineSegment(sketch, "E281", {"start": v(-10.27, -52.37) * mm, "end": v(-9.8, -52.37) * mm});
            skLineSegment(sketch, "E282", {"start": v(-9.8, -52.37) * mm, "end": v(-9.33, -52.37) * mm});
            skLineSegment(sketch, "E283", {"start": v(-9.33, -52.37) * mm, "end": v(-8.86, -52.37) * mm});
            skLineSegment(sketch, "E284", {"start": v(-8.86, -52.37) * mm, "end": v(-8.39, -52.37) * mm});
            skLineSegment(sketch, "E285", {"start": v(-8.39, -52.37) * mm, "end": v(-7.92, -52.37) * mm});
            skLineSegment(sketch, "E286", {"start": v(-7.92, -52.37) * mm, "end": v(-7.45, -52.37) * mm});
            skLineSegment(sketch, "E287", {"start": v(-7.45, -52.37) * mm, "end": v(-7.45, -52) * mm});
            skLineSegment(sketch, "E288", {"start": v(-7.45, -52) * mm, "end": v(-7.45, -51.64) * mm});
            skLineSegment(sketch, "E289", {"start": v(-7.45, -51.64) * mm, "end": v(-7.45, -51.28) * mm});
            skLineSegment(sketch, "E290", {"start": v(-7.45, -51.28) * mm, "end": v(-7.45, -50.92) * mm});
            skLineSegment(sketch, "E291", {"start": v(-7.45, -50.92) * mm, "end": v(-7.45, -50.56) * mm});
            skLineSegment(sketch, "E292", {"start": v(-7.45, -50.56) * mm, "end": v(-7.45, -50.2) * mm});
            skLineSegment(sketch, "E293", {"start": v(-7.45, -50.2) * mm, "end": v(-7.45, -49.84) * mm});
            skLineSegment(sketch, "E294", {"start": v(-7.45, -49.84) * mm, "end": v(-7.45, -49.47) * mm});
            skLineSegment(sketch, "E295", {"start": v(-7.45, -49.47) * mm, "end": v(-7.45, -49.11) * mm});
            skLineSegment(sketch, "E296", {"start": v(-7.45, -49.11) * mm, "end": v(-7.45, -48.75) * mm});
            skLineSegment(sketch, "E297", {"start": v(-7.45, -48.75) * mm, "end": v(-7.45, -48.39) * mm});
            skLineSegment(sketch, "E298", {"start": v(-7.45, -48.39) * mm, "end": v(-7.45, -48.03) * mm});
            skLineSegment(sketch, "E299", {"start": v(-7.45, -48.03) * mm, "end": v(-7.45, -47.67) * mm});
            skLineSegment(sketch, "E300", {"start": v(-7.45, -47.67) * mm, "end": v(-7.45, -47.3) * mm});
            skLineSegment(sketch, "E301", {"start": v(-7.45, -47.3) * mm, "end": v(-7.45, -46.94) * mm});
            skLineSegment(sketch, "E302", {"start": v(-7.45, -46.94) * mm, "end": v(-7.45, -46.58) * mm});
            skLineSegment(sketch, "E303", {"start": v(-7.45, -46.58) * mm, "end": v(-7.45, -46.22) * mm});
            skLineSegment(sketch, "E304", {"start": v(-7.45, -46.22) * mm, "end": v(-7.45, -45.86) * mm});
            skLineSegment(sketch, "E305", {"start": v(-7.45, -45.86) * mm, "end": v(-7.45, -45.5) * mm});
            skLineSegment(sketch, "E306", {"start": v(-7.45, -45.5) * mm, "end": v(-7.45, -45.14) * mm});
            skLineSegment(sketch, "E307", {"start": v(-7.45, -45.14) * mm, "end": v(-7.45, -44.77) * mm});
            skLineSegment(sketch, "E308", {"start": v(-7.45, -44.77) * mm, "end": v(-7.45, -44.41) * mm});
            skLineSegment(sketch, "E309", {"start": v(-7.45, -44.41) * mm, "end": v(-7.45, -44.05) * mm});
            skLineSegment(sketch, "E310", {"start": v(-7.45, -44.05) * mm, "end": v(-7.45, -43.69) * mm});
            skLineSegment(sketch, "E311", {"start": v(-7.45, -43.69) * mm, "end": v(-7.45, -43.33) * mm});
            skLineSegment(sketch, "E312", {"start": v(-7.45, -43.33) * mm, "end": v(-7.45, -42.97) * mm});
            skLineSegment(sketch, "E313", {"start": v(-7.45, -42.97) * mm, "end": v(-7.45, -42.6) * mm});
            skLineSegment(sketch, "E314", {"start": v(-7.45, -42.6) * mm, "end": v(-7.45, -42.24) * mm});
            skLineSegment(sketch, "E315", {"start": v(-7.45, -42.24) * mm, "end": v(-7.45, -41.88) * mm});
            skLineSegment(sketch, "E316", {"start": v(-7.45, -41.88) * mm, "end": v(-7.45, -41.52) * mm});
            skLineSegment(sketch, "E317", {"start": v(-7.45, -41.52) * mm, "end": v(-7.45, -41.16) * mm});
            skLineSegment(sketch, "E318", {"start": v(-7.45, -41.16) * mm, "end": v(-7.45, -40.8) * mm});
            skLineSegment(sketch, "E319", {"start": v(-7.45, -40.8) * mm, "end": v(-7.44, -40.46) * mm});
            skLineSegment(sketch, "E320", {"start": v(-7.44, -40.46) * mm, "end": v(-7.42, -40.12) * mm});
            skLineSegment(sketch, "E321", {"start": v(-7.42, -40.12) * mm, "end": v(-7.38, -39.78) * mm});
            skLineSegment(sketch, "E322", {"start": v(-7.38, -39.78) * mm, "end": v(-7.33, -39.46) * mm});
            skLineSegment(sketch, "E323", {"start": v(-7.33, -39.46) * mm, "end": v(-7.26, -39.13) * mm});
            skLineSegment(sketch, "E324", {"start": v(-7.26, -39.13) * mm, "end": v(-7.18, -38.81) * mm});
            skLineSegment(sketch, "E325", {"start": v(-7.18, -38.81) * mm, "end": v(-7.09, -38.5) * mm});
            skLineSegment(sketch, "E326", {"start": v(-7.09, -38.5) * mm, "end": v(-6.98, -38.2) * mm});
            skLineSegment(sketch, "E327", {"start": v(-6.98, -38.2) * mm, "end": v(-6.86, -37.9) * mm});
            skLineSegment(sketch, "E328", {"start": v(-6.86, -37.9) * mm, "end": v(-6.73, -37.6) * mm});
            skLineSegment(sketch, "E329", {"start": v(-6.73, -37.6) * mm, "end": v(-6.58, -37.31) * mm});
            skLineSegment(sketch, "E330", {"start": v(-6.58, -37.31) * mm, "end": v(-6.43, -37.03) * mm});
            skLineSegment(sketch, "E331", {"start": v(-6.43, -37.03) * mm, "end": v(-6.26, -36.76) * mm});
            skLineSegment(sketch, "E332", {"start": v(-6.26, -36.76) * mm, "end": v(-6.08, -36.5) * mm});
            skLineSegment(sketch, "E333", {"start": v(-6.08, -36.5) * mm, "end": v(-5.89, -36.24) * mm});
            skLineSegment(sketch, "E334", {"start": v(-5.89, -36.24) * mm, "end": v(-5.69, -36) * mm});
            skLineSegment(sketch, "E335", {"start": v(-5.69, -36) * mm, "end": v(-5.48, -35.75) * mm});
            skLineSegment(sketch, "E336", {"start": v(-5.48, -35.75) * mm, "end": v(-5.26, -35.52) * mm});
            skLineSegment(sketch, "E337", {"start": v(-5.26, -35.52) * mm, "end": v(-5.03, -35.3) * mm});
            skLineSegment(sketch, "E338", {"start": v(-5.03, -35.3) * mm, "end": v(-4.79, -35.1) * mm});
            skLineSegment(sketch, "E339", {"start": v(-4.79, -35.1) * mm, "end": v(-4.54, -34.9) * mm});
            skLineSegment(sketch, "E340", {"start": v(-4.54, -34.9) * mm, "end": v(-4.28, -34.7) * mm});
            skLineSegment(sketch, "E341", {"start": v(-4.28, -34.7) * mm, "end": v(-4.02, -34.53) * mm});
            skLineSegment(sketch, "E342", {"start": v(-4.02, -34.53) * mm, "end": v(-3.74, -34.36) * mm});
            skLineSegment(sketch, "E343", {"start": v(-3.74, -34.36) * mm, "end": v(-3.46, -34.2) * mm});
            skLineSegment(sketch, "E344", {"start": v(-3.46, -34.2) * mm, "end": v(-3.18, -34.06) * mm});
            skLineSegment(sketch, "E345", {"start": v(-3.18, -34.06) * mm, "end": v(-2.88, -33.93) * mm});
            skLineSegment(sketch, "E346", {"start": v(-2.88, -33.93) * mm, "end": v(-2.58, -33.81) * mm});
            skLineSegment(sketch, "E347", {"start": v(-2.58, -33.81) * mm, "end": v(-2.27, -33.7) * mm});
            skLineSegment(sketch, "E348", {"start": v(-2.27, -33.7) * mm, "end": v(-1.96, -33.61) * mm});
            skLineSegment(sketch, "E349", {"start": v(-1.96, -33.61) * mm, "end": v(-1.64, -33.53) * mm});
            skLineSegment(sketch, "E350", {"start": v(-1.64, -33.53) * mm, "end": v(-1.32, -33.47) * mm});
            skLineSegment(sketch, "E351", {"start": v(-1.32, -33.47) * mm, "end": v(-1.3, -33.44) * mm});
            skLineSegment(sketch, "E352", {"start": v(-1.3, -33.44) * mm, "end": v(-1.3, -33.42) * mm});
            skLineSegment(sketch, "E353", {"start": v(-1.3, -33.42) * mm, "end": v(-1.28, -33.4) * mm});
            skLineSegment(sketch, "E354", {"start": v(-1.28, -33.4) * mm, "end": v(-1.26, -33.37) * mm});
            skLineSegment(sketch, "E355", {"start": v(-1.26, -33.37) * mm, "end": v(-1.25, -33.34) * mm});
            skLineSegment(sketch, "E356", {"start": v(-1.25, -33.34) * mm, "end": v(-1.23, -33.32) * mm});
            skLineSegment(sketch, "E357", {"start": v(-1.23, -33.32) * mm, "end": v(-1.22, -33.3) * mm});
            skLineSegment(sketch, "E358", {"start": v(-1.22, -33.3) * mm, "end": v(-1.2, -33.27) * mm});
            skLineSegment(sketch, "E359", {"start": v(-1.2, -33.27) * mm, "end": v(-1.18, -33.25) * mm});
            skLineSegment(sketch, "E360", {"start": v(-1.18, -33.25) * mm, "end": v(-1.16, -33.23) * mm});
            skLineSegment(sketch, "E361", {"start": v(-1.16, -33.23) * mm, "end": v(-1.14, -33.2) * mm});
            skLineSegment(sketch, "E362", {"start": v(-1.14, -33.2) * mm, "end": v(-1.12, -33.18) * mm});
            skLineSegment(sketch, "E363", {"start": v(-1.12, -33.18) * mm, "end": v(-1.1, -33.16) * mm});
            skLineSegment(sketch, "E364", {"start": v(-1.1, -33.16) * mm, "end": v(-1.08, -33.14) * mm});
            skLineSegment(sketch, "E365", {"start": v(-1.08, -33.14) * mm, "end": v(-1.05, -33.12) * mm});
            skLineSegment(sketch, "E366", {"start": v(-1.05, -33.12) * mm, "end": v(-1.03, -33.1) * mm});
            skLineSegment(sketch, "E367", {"start": v(-1.03, -33.1) * mm, "end": v(-1, -33.08) * mm});
            skLineSegment(sketch, "E368", {"start": v(-1, -33.08) * mm, "end": v(-0.98, -33.06) * mm});
            skLineSegment(sketch, "E369", {"start": v(-0.98, -33.06) * mm, "end": v(-0.95, -33.04) * mm});
            skLineSegment(sketch, "E370", {"start": v(-0.95, -33.04) * mm, "end": v(-0.93, -33.03) * mm});
            skLineSegment(sketch, "E371", {"start": v(-0.93, -33.03) * mm, "end": v(-0.9, -33) * mm});
            skLineSegment(sketch, "E372", {"start": v(-0.9, -33) * mm, "end": v(-0.87, -33) * mm});
            skLineSegment(sketch, "E373", {"start": v(-0.87, -33) * mm, "end": v(-0.84, -32.97) * mm});
            skLineSegment(sketch, "E374", {"start": v(-0.84, -32.97) * mm, "end": v(-0.81, -32.96) * mm});
            skLineSegment(sketch, "E375", {"start": v(-0.81, -32.96) * mm, "end": v(-0.78, -32.94) * mm});
            skLineSegment(sketch, "E376", {"start": v(-0.78, -32.94) * mm, "end": v(-0.75, -32.93) * mm});
            skLineSegment(sketch, "E377", {"start": v(-0.75, -32.93) * mm, "end": v(-0.72, -32.91) * mm});
            skLineSegment(sketch, "E378", {"start": v(-0.72, -32.91) * mm, "end": v(-0.7, -32.9) * mm});
            skLineSegment(sketch, "E379", {"start": v(-0.7, -32.9) * mm, "end": v(-0.66, -32.89) * mm});
            skLineSegment(sketch, "E380", {"start": v(-0.66, -32.89) * mm, "end": v(-0.63, -32.88) * mm});
            skLineSegment(sketch, "E381", {"start": v(-0.63, -32.88) * mm, "end": v(-0.6, -32.86) * mm});
            skLineSegment(sketch, "E382", {"start": v(-0.6, -32.86) * mm, "end": v(-0.56, -32.85) * mm});
            skLineSegment(sketch, "E383", {"start": v(-0.56, -32.85) * mm, "end": v(-0.56, -32.84) * mm});
            skLineSegment(sketch, "E384", {"start": v(-0.56, -32.84) * mm, "end": v(-0.56, -32.82) * mm});
            skLineSegment(sketch, "E385", {"start": v(-0.56, -32.82) * mm, "end": v(-0.56, -32.8) * mm});
            skLineSegment(sketch, "E386", {"start": v(-0.56, -32.8) * mm, "end": v(-0.56, -32.8) * mm});
            skLineSegment(sketch, "E387", {"start": v(-0.56, -32.8) * mm, "end": v(-0.56, -32.78) * mm});
            skLineSegment(sketch, "E388", {"start": v(-0.56, -32.78) * mm, "end": v(-0.56, -32.77) * mm});
            skLineSegment(sketch, "E389", {"start": v(-0.56, -32.77) * mm, "end": v(-0.56, -32.75) * mm});
            skLineSegment(sketch, "E390", {"start": v(-0.56, -32.75) * mm, "end": v(-0.56, -32.74) * mm});
            skLineSegment(sketch, "E391", {"start": v(-0.56, -32.74) * mm, "end": v(-0.56, -32.72) * mm});
            skLineSegment(sketch, "E392", {"start": v(-0.56, -32.72) * mm, "end": v(-0.56, -32.7) * mm});
            skLineSegment(sketch, "E393", {"start": v(-0.56, -32.7) * mm, "end": v(-0.56, -32.7) * mm});
            skLineSegment(sketch, "E394", {"start": v(-0.56, -32.7) * mm, "end": v(-0.56, -32.68) * mm});
            skLineSegment(sketch, "E395", {"start": v(-0.56, -32.68) * mm, "end": v(-0.56, -32.67) * mm});
            skLineSegment(sketch, "E396", {"start": v(-0.56, -32.67) * mm, "end": v(-0.56, -32.65) * mm});
            skLineSegment(sketch, "E397", {"start": v(-0.56, -32.65) * mm, "end": v(-0.56, -32.64) * mm});
            skLineSegment(sketch, "E398", {"start": v(-0.56, -32.64) * mm, "end": v(-0.56, -32.62) * mm});
            skLineSegment(sketch, "E399", {"start": v(-0.56, -32.62) * mm, "end": v(-0.56, -32.6) * mm});
            skLineSegment(sketch, "E400", {"start": v(-0.56, -32.6) * mm, "end": v(-0.56, -32.6) * mm});
            skLineSegment(sketch, "E401", {"start": v(-0.56, -32.6) * mm, "end": v(-0.56, -32.58) * mm});
            skLineSegment(sketch, "E402", {"start": v(-0.56, -32.58) * mm, "end": v(-0.56, -32.56) * mm});
            skLineSegment(sketch, "E403", {"start": v(-0.56, -32.56) * mm, "end": v(-0.56, -32.55) * mm});
            skLineSegment(sketch, "E404", {"start": v(-0.56, -32.55) * mm, "end": v(-0.56, -32.54) * mm});
            skLineSegment(sketch, "E405", {"start": v(-0.56, -32.54) * mm, "end": v(-0.56, -32.52) * mm});
            skLineSegment(sketch, "E406", {"start": v(-0.56, -32.52) * mm, "end": v(-0.56, -32.5) * mm});
            skLineSegment(sketch, "E407", {"start": v(-0.56, -32.5) * mm, "end": v(-0.56, -32.5) * mm});
            skLineSegment(sketch, "E408", {"start": v(-0.56, -32.5) * mm, "end": v(-0.56, -32.48) * mm});
            skLineSegment(sketch, "E409", {"start": v(-0.56, -32.48) * mm, "end": v(-0.56, -32.46) * mm});
            skLineSegment(sketch, "E410", {"start": v(-0.56, -32.46) * mm, "end": v(-0.56, -32.45) * mm});
            skLineSegment(sketch, "E411", {"start": v(-0.56, -32.45) * mm, "end": v(-0.56, -32.43) * mm});
            skLineSegment(sketch, "E412", {"start": v(-0.56, -32.43) * mm, "end": v(-0.56, -32.42) * mm});
            skLineSegment(sketch, "E413", {"start": v(-0.56, -32.42) * mm, "end": v(-0.56, -32.4) * mm});
            skLineSegment(sketch, "E414", {"start": v(-0.56, -32.4) * mm, "end": v(-0.56, -32.4) * mm});
            skLineSegment(sketch, "E415", {"start": v(-0.56, -32.4) * mm, "end": v(-0.56, -32.36) * mm});
            skLineSegment(sketch, "E416", {"start": v(-0.56, -32.36) * mm, "end": v(-0.56, -32.33) * mm});
            skLineSegment(sketch, "E417", {"start": v(-0.56, -32.33) * mm, "end": v(-0.56, -32.3) * mm});
            skLineSegment(sketch, "E418", {"start": v(-0.56, -32.3) * mm, "end": v(-0.55, -32.28) * mm});
            skLineSegment(sketch, "E419", {"start": v(-0.55, -32.28) * mm, "end": v(-0.54, -32.25) * mm});
            skLineSegment(sketch, "E420", {"start": v(-0.54, -32.25) * mm, "end": v(-0.54, -32.22) * mm});
            skLineSegment(sketch, "E421", {"start": v(-0.54, -32.22) * mm, "end": v(-0.53, -32.2) * mm});
            skLineSegment(sketch, "E422", {"start": v(-0.53, -32.2) * mm, "end": v(-0.52, -32.17) * mm});
            skLineSegment(sketch, "E423", {"start": v(-0.52, -32.17) * mm, "end": v(-0.5, -32.15) * mm});
            skLineSegment(sketch, "E424", {"start": v(-0.5, -32.15) * mm, "end": v(-0.5, -32.12) * mm});
            skLineSegment(sketch, "E425", {"start": v(-0.5, -32.12) * mm, "end": v(-0.48, -32.1) * mm});
            skLineSegment(sketch, "E426", {"start": v(-0.48, -32.1) * mm, "end": v(-0.47, -32.08) * mm});
            skLineSegment(sketch, "E427", {"start": v(-0.47, -32.08) * mm, "end": v(-0.45, -32.06) * mm});
            skLineSegment(sketch, "E428", {"start": v(-0.45, -32.06) * mm, "end": v(-0.43, -32.03) * mm});
            skLineSegment(sketch, "E429", {"start": v(-0.43, -32.03) * mm, "end": v(-0.42, -32.01) * mm});
            skLineSegment(sketch, "E430", {"start": v(-0.42, -32.01) * mm, "end": v(-0.4, -32) * mm});
            skLineSegment(sketch, "E431", {"start": v(-0.4, -32) * mm, "end": v(-0.38, -31.98) * mm});
            skLineSegment(sketch, "E432", {"start": v(-0.38, -31.98) * mm, "end": v(-0.36, -31.96) * mm});
            skLineSegment(sketch, "E433", {"start": v(-0.36, -31.96) * mm, "end": v(-0.34, -31.94) * mm});
            skLineSegment(sketch, "E434", {"start": v(-0.34, -31.94) * mm, "end": v(-0.31, -31.93) * mm});
            skLineSegment(sketch, "E435", {"start": v(-0.31, -31.93) * mm, "end": v(-0.3, -31.91) * mm});
            skLineSegment(sketch, "E436", {"start": v(-0.3, -31.91) * mm, "end": v(-0.27, -31.9) * mm});
            skLineSegment(sketch, "E437", {"start": v(-0.27, -31.9) * mm, "end": v(-0.24, -31.89) * mm});
            skLineSegment(sketch, "E438", {"start": v(-0.24, -31.89) * mm, "end": v(-0.22, -31.87) * mm});
            skLineSegment(sketch, "E439", {"start": v(-0.22, -31.87) * mm, "end": v(-0.2, -31.86) * mm});
            skLineSegment(sketch, "E440", {"start": v(-0.2, -31.86) * mm, "end": v(-0.17, -31.86) * mm});
            skLineSegment(sketch, "E441", {"start": v(-0.17, -31.86) * mm, "end": v(-0.14, -31.85) * mm});
            skLineSegment(sketch, "E442", {"start": v(-0.14, -31.85) * mm, "end": v(-0.11, -31.84) * mm});
            skLineSegment(sketch, "E443", {"start": v(-0.11, -31.84) * mm, "end": v(-0.09, -31.84) * mm});
            skLineSegment(sketch, "E444", {"start": v(-0.09, -31.84) * mm, "end": v(-0.06, -31.83) * mm});
            skLineSegment(sketch, "E445", {"start": v(-0.06, -31.83) * mm, "end": v(-0.03, -31.83) * mm});
            skLineSegment(sketch, "E446", {"start": v(-0.03, -31.83) * mm, "end": v(0, -31.83) * mm});
            skLineSegment(sketch, "E447", {"start": v(0.06, -31.83) * mm, "end": v(0.09, -31.84) * mm});
            skLineSegment(sketch, "E448", {"start": v(0.09, -31.84) * mm, "end": v(0.11, -31.84) * mm});
            skLineSegment(sketch, "E449", {"start": v(0.11, -31.84) * mm, "end": v(0.14, -31.85) * mm});
            skLineSegment(sketch, "E450", {"start": v(0.14, -31.85) * mm, "end": v(0.17, -31.86) * mm});
            skLineSegment(sketch, "E451", {"start": v(0.17, -31.86) * mm, "end": v(0.2, -31.86) * mm});
            skLineSegment(sketch, "E452", {"start": v(0.2, -31.86) * mm, "end": v(0.22, -31.87) * mm});
            skLineSegment(sketch, "E453", {"start": v(0.22, -31.87) * mm, "end": v(0.24, -31.89) * mm});
            skLineSegment(sketch, "E454", {"start": v(0.24, -31.89) * mm, "end": v(0.27, -31.9) * mm});
            skLineSegment(sketch, "E455", {"start": v(0.27, -31.9) * mm, "end": v(0.3, -31.91) * mm});
            skLineSegment(sketch, "E456", {"start": v(0.3, -31.91) * mm, "end": v(0.31, -31.93) * mm});
            skLineSegment(sketch, "E457", {"start": v(0.31, -31.93) * mm, "end": v(0.34, -31.94) * mm});
            skLineSegment(sketch, "E458", {"start": v(0.34, -31.94) * mm, "end": v(0.36, -31.96) * mm});
            skLineSegment(sketch, "E459", {"start": v(0.36, -31.96) * mm, "end": v(0.38, -31.98) * mm});
            skLineSegment(sketch, "E460", {"start": v(0.38, -31.98) * mm, "end": v(0.4, -32) * mm});
            skLineSegment(sketch, "E461", {"start": v(0.4, -32) * mm, "end": v(0.42, -32.01) * mm});
            skLineSegment(sketch, "E462", {"start": v(0.42, -32.01) * mm, "end": v(0.43, -32.03) * mm});
            skLineSegment(sketch, "E463", {"start": v(0.43, -32.03) * mm, "end": v(0.45, -32.06) * mm});
            skLineSegment(sketch, "E464", {"start": v(0.45, -32.06) * mm, "end": v(0.47, -32.08) * mm});
            skLineSegment(sketch, "E465", {"start": v(0.47, -32.08) * mm, "end": v(0.48, -32.1) * mm});
            skLineSegment(sketch, "E466", {"start": v(0.48, -32.1) * mm, "end": v(0.5, -32.12) * mm});
            skLineSegment(sketch, "E467", {"start": v(0.5, -32.12) * mm, "end": v(0.5, -32.15) * mm});
            skLineSegment(sketch, "E468", {"start": v(0.5, -32.15) * mm, "end": v(0.52, -32.17) * mm});
            skLineSegment(sketch, "E469", {"start": v(0.52, -32.17) * mm, "end": v(0.53, -32.2) * mm});
            skLineSegment(sketch, "E470", {"start": v(0.53, -32.2) * mm, "end": v(0.54, -32.22) * mm});
            skLineSegment(sketch, "E471", {"start": v(0.54, -32.22) * mm, "end": v(0.54, -32.25) * mm});
            skLineSegment(sketch, "E472", {"start": v(0.54, -32.25) * mm, "end": v(0.55, -32.28) * mm});
            skLineSegment(sketch, "E473", {"start": v(0.55, -32.28) * mm, "end": v(0.55, -32.3) * mm});
            skLineSegment(sketch, "E474", {"start": v(0.55, -32.3) * mm, "end": v(0.56, -32.33) * mm});
            skLineSegment(sketch, "E475", {"start": v(0.56, -32.33) * mm, "end": v(0.56, -32.36) * mm});
            skLineSegment(sketch, "E476", {"start": v(0.56, -32.36) * mm, "end": v(0.56, -32.4) * mm});
            skLineSegment(sketch, "E477", {"start": v(0.56, -32.4) * mm, "end": v(0.56, -32.4) * mm});
            skLineSegment(sketch, "E478", {"start": v(0.56, -32.4) * mm, "end": v(0.56, -32.42) * mm});
            skLineSegment(sketch, "E479", {"start": v(0.56, -32.42) * mm, "end": v(0.56, -32.43) * mm});
            skLineSegment(sketch, "E480", {"start": v(0.56, -32.43) * mm, "end": v(0.56, -32.45) * mm});
            skLineSegment(sketch, "E481", {"start": v(0.56, -32.45) * mm, "end": v(0.56, -32.46) * mm});
            skLineSegment(sketch, "E482", {"start": v(0.56, -32.46) * mm, "end": v(0.56, -32.48) * mm});
            skLineSegment(sketch, "E483", {"start": v(0.56, -32.48) * mm, "end": v(0.56, -32.5) * mm});
            skLineSegment(sketch, "E484", {"start": v(0.56, -32.5) * mm, "end": v(0.56, -32.5) * mm});
            skLineSegment(sketch, "E485", {"start": v(0.56, -32.5) * mm, "end": v(0.56, -32.52) * mm});
            skLineSegment(sketch, "E486", {"start": v(0.56, -32.52) * mm, "end": v(0.56, -32.54) * mm});
            skLineSegment(sketch, "E487", {"start": v(0.56, -32.54) * mm, "end": v(0.56, -32.55) * mm});
            skLineSegment(sketch, "E488", {"start": v(0.56, -32.55) * mm, "end": v(0.56, -32.56) * mm});
            skLineSegment(sketch, "E489", {"start": v(0.56, -32.56) * mm, "end": v(0.56, -32.58) * mm});
            skLineSegment(sketch, "E490", {"start": v(0.56, -32.58) * mm, "end": v(0.56, -32.6) * mm});
            skLineSegment(sketch, "E491", {"start": v(0.56, -32.6) * mm, "end": v(0.56, -32.6) * mm});
            skLineSegment(sketch, "E492", {"start": v(0.56, -32.6) * mm, "end": v(0.56, -32.62) * mm});
            skLineSegment(sketch, "E493", {"start": v(0.56, -32.62) * mm, "end": v(0.56, -32.64) * mm});
            skLineSegment(sketch, "E494", {"start": v(0.56, -32.64) * mm, "end": v(0.56, -32.65) * mm});
            skLineSegment(sketch, "E495", {"start": v(0.56, -32.65) * mm, "end": v(0.56, -32.67) * mm});
            skLineSegment(sketch, "E496", {"start": v(0.56, -32.67) * mm, "end": v(0.56, -32.68) * mm});
            skLineSegment(sketch, "E497", {"start": v(0.56, -32.68) * mm, "end": v(0.56, -32.7) * mm});
            skLineSegment(sketch, "E498", {"start": v(0.56, -32.7) * mm, "end": v(0.56, -32.7) * mm});
            skLineSegment(sketch, "E499", {"start": v(0.56, -32.7) * mm, "end": v(0.56, -32.72) * mm});
            skLineSegment(sketch, "E500", {"start": v(0.56, -32.72) * mm, "end": v(0.56, -32.74) * mm});
            skLineSegment(sketch, "E501", {"start": v(0.56, -32.74) * mm, "end": v(0.56, -32.75) * mm});
            skLineSegment(sketch, "E502", {"start": v(0.56, -32.75) * mm, "end": v(0.56, -32.77) * mm});
            skLineSegment(sketch, "E503", {"start": v(0.56, -32.77) * mm, "end": v(0.56, -32.78) * mm});
            skLineSegment(sketch, "E504", {"start": v(0.56, -32.78) * mm, "end": v(0.56, -32.8) * mm});
            skLineSegment(sketch, "E505", {"start": v(0.56, -32.8) * mm, "end": v(0.56, -32.8) * mm});
            skLineSegment(sketch, "E506", {"start": v(0.56, -32.8) * mm, "end": v(0.56, -32.82) * mm});
            skLineSegment(sketch, "E507", {"start": v(0.56, -32.82) * mm, "end": v(0.56, -32.84) * mm});
            skLineSegment(sketch, "E508", {"start": v(0.56, -32.84) * mm, "end": v(0.56, -32.85) * mm});
            skLineSegment(sketch, "E509", {"start": v(0.56, -32.85) * mm, "end": v(0.6, -32.86) * mm});
            skLineSegment(sketch, "E510", {"start": v(0.6, -32.86) * mm, "end": v(0.63, -32.88) * mm});
            skLineSegment(sketch, "E511", {"start": v(0.63, -32.88) * mm, "end": v(0.66, -32.89) * mm});
            skLineSegment(sketch, "E512", {"start": v(0.66, -32.89) * mm, "end": v(0.7, -32.9) * mm});
            skLineSegment(sketch, "E513", {"start": v(0.7, -32.9) * mm, "end": v(0.72, -32.91) * mm});
            skLineSegment(sketch, "E514", {"start": v(0.72, -32.91) * mm, "end": v(0.75, -32.93) * mm});
            skLineSegment(sketch, "E515", {"start": v(0.75, -32.93) * mm, "end": v(0.78, -32.94) * mm});
            skLineSegment(sketch, "E516", {"start": v(0.78, -32.94) * mm, "end": v(0.81, -32.96) * mm});
            skLineSegment(sketch, "E517", {"start": v(0.81, -32.96) * mm, "end": v(0.84, -32.97) * mm});
            skLineSegment(sketch, "E518", {"start": v(0.84, -32.97) * mm, "end": v(0.87, -33) * mm});
            skLineSegment(sketch, "E519", {"start": v(0.87, -33) * mm, "end": v(0.9, -33) * mm});
            skLineSegment(sketch, "E520", {"start": v(0.9, -33) * mm, "end": v(0.93, -33.03) * mm});
            skLineSegment(sketch, "E521", {"start": v(0.93, -33.03) * mm, "end": v(0.95, -33.04) * mm});
            skLineSegment(sketch, "E522", {"start": v(0.95, -33.04) * mm, "end": v(0.98, -33.06) * mm});
            skLineSegment(sketch, "E523", {"start": v(0.98, -33.06) * mm, "end": v(1, -33.08) * mm});
            skLineSegment(sketch, "E524", {"start": v(1, -33.08) * mm, "end": v(1.03, -33.1) * mm});
            skLineSegment(sketch, "E525", {"start": v(1.03, -33.1) * mm, "end": v(1.05, -33.12) * mm});
            skLineSegment(sketch, "E526", {"start": v(1.05, -33.12) * mm, "end": v(1.08, -33.14) * mm});
            skLineSegment(sketch, "E527", {"start": v(1.08, -33.14) * mm, "end": v(1.1, -33.16) * mm});
            skLineSegment(sketch, "E528", {"start": v(1.1, -33.16) * mm, "end": v(1.12, -33.18) * mm});
            skLineSegment(sketch, "E529", {"start": v(1.12, -33.18) * mm, "end": v(1.14, -33.2) * mm});
            skLineSegment(sketch, "E530", {"start": v(1.14, -33.2) * mm, "end": v(1.16, -33.23) * mm});
            skLineSegment(sketch, "E531", {"start": v(1.16, -33.23) * mm, "end": v(1.18, -33.25) * mm});
            skLineSegment(sketch, "E532", {"start": v(1.18, -33.25) * mm, "end": v(1.2, -33.27) * mm});
            skLineSegment(sketch, "E533", {"start": v(1.2, -33.27) * mm, "end": v(1.22, -33.3) * mm});
            skLineSegment(sketch, "E534", {"start": v(1.22, -33.3) * mm, "end": v(1.23, -33.32) * mm});
            skLineSegment(sketch, "E535", {"start": v(1.23, -33.32) * mm, "end": v(1.25, -33.34) * mm});
            skLineSegment(sketch, "E536", {"start": v(1.25, -33.34) * mm, "end": v(1.26, -33.37) * mm});
            skLineSegment(sketch, "E537", {"start": v(1.26, -33.37) * mm, "end": v(1.28, -33.4) * mm});
            skLineSegment(sketch, "E538", {"start": v(1.28, -33.4) * mm, "end": v(1.3, -33.42) * mm});
            skLineSegment(sketch, "E539", {"start": v(1.3, -33.42) * mm, "end": v(1.3, -33.44) * mm});
            skLineSegment(sketch, "E540", {"start": v(1.3, -33.44) * mm, "end": v(1.32, -33.47) * mm});
            skLineSegment(sketch, "E541", {"start": v(1.32, -33.47) * mm, "end": v(1.64, -33.53) * mm});
            skLineSegment(sketch, "E542", {"start": v(1.64, -33.53) * mm, "end": v(1.96, -33.61) * mm});
            skLineSegment(sketch, "E543", {"start": v(1.96, -33.61) * mm, "end": v(2.27, -33.7) * mm});
            skLineSegment(sketch, "E544", {"start": v(2.27, -33.7) * mm, "end": v(2.58, -33.81) * mm});
            skLineSegment(sketch, "E545", {"start": v(2.58, -33.81) * mm, "end": v(2.88, -33.93) * mm});
            skLineSegment(sketch, "E546", {"start": v(2.88, -33.93) * mm, "end": v(3.18, -34.06) * mm});
            skLineSegment(sketch, "E547", {"start": v(3.18, -34.06) * mm, "end": v(3.46, -34.2) * mm});
            skLineSegment(sketch, "E548", {"start": v(3.46, -34.2) * mm, "end": v(3.74, -34.36) * mm});
            skLineSegment(sketch, "E549", {"start": v(3.74, -34.36) * mm, "end": v(4.02, -34.53) * mm});
            skLineSegment(sketch, "E550", {"start": v(4.02, -34.53) * mm, "end": v(4.28, -34.7) * mm});
            skLineSegment(sketch, "E551", {"start": v(4.28, -34.7) * mm, "end": v(4.54, -34.9) * mm});
            skLineSegment(sketch, "E552", {"start": v(4.54, -34.9) * mm, "end": v(4.79, -35.1) * mm});
            skLineSegment(sketch, "E553", {"start": v(4.79, -35.1) * mm, "end": v(5.03, -35.3) * mm});
            skLineSegment(sketch, "E554", {"start": v(5.03, -35.3) * mm, "end": v(5.26, -35.52) * mm});
            skLineSegment(sketch, "E555", {"start": v(5.26, -35.52) * mm, "end": v(5.48, -35.75) * mm});
            skLineSegment(sketch, "E556", {"start": v(5.48, -35.75) * mm, "end": v(5.69, -36) * mm});
            skLineSegment(sketch, "E557", {"start": v(5.69, -36) * mm, "end": v(5.89, -36.24) * mm});
            skLineSegment(sketch, "E558", {"start": v(5.89, -36.24) * mm, "end": v(6.08, -36.5) * mm});
            skLineSegment(sketch, "E559", {"start": v(6.08, -36.5) * mm, "end": v(6.26, -36.76) * mm});
            skLineSegment(sketch, "E560", {"start": v(6.26, -36.76) * mm, "end": v(6.43, -37.03) * mm});
            skLineSegment(sketch, "E561", {"start": v(6.43, -37.03) * mm, "end": v(6.58, -37.31) * mm});
            skLineSegment(sketch, "E562", {"start": v(6.58, -37.31) * mm, "end": v(6.73, -37.6) * mm});
            skLineSegment(sketch, "E563", {"start": v(6.73, -37.6) * mm, "end": v(6.86, -37.9) * mm});
            skLineSegment(sketch, "E564", {"start": v(6.86, -37.9) * mm, "end": v(6.98, -38.2) * mm});
            skLineSegment(sketch, "E565", {"start": v(6.98, -38.2) * mm, "end": v(7.09, -38.5) * mm});
            skLineSegment(sketch, "E566", {"start": v(7.09, -38.5) * mm, "end": v(7.18, -38.81) * mm});
            skLineSegment(sketch, "E567", {"start": v(7.18, -38.81) * mm, "end": v(7.26, -39.13) * mm});
            skLineSegment(sketch, "E568", {"start": v(7.26, -39.13) * mm, "end": v(7.33, -39.46) * mm});
            skLineSegment(sketch, "E569", {"start": v(7.33, -39.46) * mm, "end": v(7.38, -39.78) * mm});
            skLineSegment(sketch, "E570", {"start": v(7.38, -39.78) * mm, "end": v(7.42, -40.12) * mm});
            skLineSegment(sketch, "E571", {"start": v(7.42, -40.12) * mm, "end": v(7.44, -40.46) * mm});
            skLineSegment(sketch, "E572", {"start": v(7.44, -40.46) * mm, "end": v(7.45, -40.8) * mm});
            skLineSegment(sketch, "E573", {"start": v(7.45, -40.8) * mm, "end": v(7.45, -41.16) * mm});
            skLineSegment(sketch, "E574", {"start": v(7.45, -41.16) * mm, "end": v(7.45, -41.52) * mm});
            skLineSegment(sketch, "E575", {"start": v(7.45, -41.52) * mm, "end": v(7.45, -41.88) * mm});
            skLineSegment(sketch, "E576", {"start": v(7.45, -41.88) * mm, "end": v(7.45, -42.24) * mm});
            skLineSegment(sketch, "E577", {"start": v(7.45, -42.24) * mm, "end": v(7.45, -42.6) * mm});
            skLineSegment(sketch, "E578", {"start": v(7.45, -42.6) * mm, "end": v(7.45, -42.97) * mm});
            skLineSegment(sketch, "E579", {"start": v(7.45, -42.97) * mm, "end": v(7.45, -43.33) * mm});
            skLineSegment(sketch, "E580", {"start": v(7.45, -43.33) * mm, "end": v(7.45, -43.69) * mm});
            skLineSegment(sketch, "E581", {"start": v(7.45, -43.69) * mm, "end": v(7.45, -44.05) * mm});
            skLineSegment(sketch, "E582", {"start": v(7.45, -44.05) * mm, "end": v(7.45, -44.41) * mm});
            skLineSegment(sketch, "E583", {"start": v(7.45, -44.41) * mm, "end": v(7.45, -44.77) * mm});
            skLineSegment(sketch, "E584", {"start": v(7.45, -44.77) * mm, "end": v(7.45, -45.14) * mm});
            skLineSegment(sketch, "E585", {"start": v(7.45, -45.14) * mm, "end": v(7.45, -45.5) * mm});
            skLineSegment(sketch, "E586", {"start": v(7.45, -45.5) * mm, "end": v(7.45, -45.86) * mm});
            skLineSegment(sketch, "E587", {"start": v(7.45, -45.86) * mm, "end": v(7.45, -46.22) * mm});
            skLineSegment(sketch, "E588", {"start": v(7.45, -46.22) * mm, "end": v(7.45, -46.58) * mm});
            skLineSegment(sketch, "E589", {"start": v(7.45, -46.58) * mm, "end": v(7.45, -46.94) * mm});
            skLineSegment(sketch, "E590", {"start": v(7.45, -46.94) * mm, "end": v(7.45, -47.3) * mm});
            skLineSegment(sketch, "E591", {"start": v(7.45, -47.3) * mm, "end": v(7.45, -47.67) * mm});
            skLineSegment(sketch, "E592", {"start": v(7.45, -47.67) * mm, "end": v(7.45, -48.03) * mm});
            skLineSegment(sketch, "E593", {"start": v(7.45, -48.03) * mm, "end": v(7.45, -48.39) * mm});
            skLineSegment(sketch, "E594", {"start": v(7.45, -48.39) * mm, "end": v(7.45, -48.75) * mm});
            skLineSegment(sketch, "E595", {"start": v(7.45, -48.75) * mm, "end": v(7.45, -49.11) * mm});
            skLineSegment(sketch, "E596", {"start": v(7.45, -49.11) * mm, "end": v(7.45, -49.47) * mm});
            skLineSegment(sketch, "E597", {"start": v(7.45, -49.47) * mm, "end": v(7.45, -49.84) * mm});
            skLineSegment(sketch, "E598", {"start": v(7.45, -49.84) * mm, "end": v(7.45, -50.2) * mm});
            skLineSegment(sketch, "E599", {"start": v(7.45, -50.2) * mm, "end": v(7.45, -50.56) * mm});
            skLineSegment(sketch, "E600", {"start": v(7.45, -50.56) * mm, "end": v(7.45, -50.92) * mm});
            skLineSegment(sketch, "E601", {"start": v(7.45, -50.92) * mm, "end": v(7.45, -51.28) * mm});
            skLineSegment(sketch, "E602", {"start": v(7.45, -51.28) * mm, "end": v(7.45, -51.64) * mm});
            skLineSegment(sketch, "E603", {"start": v(7.45, -51.64) * mm, "end": v(7.45, -52) * mm});
            skLineSegment(sketch, "E604", {"start": v(7.45, -52) * mm, "end": v(7.45, -52.37) * mm});
            skLineSegment(sketch, "E605", {"start": v(7.45, -52.37) * mm, "end": v(7.92, -52.37) * mm});
            skLineSegment(sketch, "E606", {"start": v(7.92, -52.37) * mm, "end": v(8.39, -52.37) * mm});
            skLineSegment(sketch, "E607", {"start": v(8.39, -52.37) * mm, "end": v(8.86, -52.37) * mm});
            skLineSegment(sketch, "E608", {"start": v(8.86, -52.37) * mm, "end": v(9.33, -52.37) * mm});
            skLineSegment(sketch, "E609", {"start": v(9.33, -52.37) * mm, "end": v(9.8, -52.37) * mm});
            skLineSegment(sketch, "E610", {"start": v(9.8, -52.37) * mm, "end": v(10.27, -52.37) * mm});
            skLineSegment(sketch, "E611", {"start": v(10.27, -52.37) * mm, "end": v(10.74, -52.37) * mm});
            skLineSegment(sketch, "E612", {"start": v(10.74, -52.37) * mm, "end": v(11.21, -52.37) * mm});
            skLineSegment(sketch, "E613", {"start": v(11.21, -52.37) * mm, "end": v(11.68, -52.37) * mm});
            skLineSegment(sketch, "E614", {"start": v(11.68, -52.37) * mm, "end": v(12.15, -52.37) * mm});
            skLineSegment(sketch, "E615", {"start": v(12.15, -52.37) * mm, "end": v(12.62, -52.37) * mm});
            skLineSegment(sketch, "E616", {"start": v(12.62, -52.37) * mm, "end": v(13.1, -52.37) * mm});
            skLineSegment(sketch, "E617", {"start": v(13.1, -52.37) * mm, "end": v(13.56, -52.37) * mm});
            skLineSegment(sketch, "E618", {"start": v(13.56, -52.37) * mm, "end": v(14.03, -52.37) * mm});
            skLineSegment(sketch, "E619", {"start": v(14.03, -52.37) * mm, "end": v(14.5, -52.37) * mm});
            skLineSegment(sketch, "E620", {"start": v(14.5, -52.37) * mm, "end": v(14.97, -52.37) * mm});
            skLineSegment(sketch, "E621", {"start": v(14.97, -52.37) * mm, "end": v(15.44, -52.37) * mm});
            skLineSegment(sketch, "E622", {"start": v(15.44, -52.37) * mm, "end": v(15.91, -52.37) * mm});
            skLineSegment(sketch, "E623", {"start": v(15.91, -52.37) * mm, "end": v(16.39, -52.37) * mm});
            skLineSegment(sketch, "E624", {"start": v(16.39, -52.37) * mm, "end": v(16.86, -52.37) * mm});
            skLineSegment(sketch, "E625", {"start": v(16.86, -52.37) * mm, "end": v(17.33, -52.37) * mm});
            skLineSegment(sketch, "E626", {"start": v(17.33, -52.37) * mm, "end": v(17.8, -52.37) * mm});
            skLineSegment(sketch, "E627", {"start": v(17.8, -52.37) * mm, "end": v(18.27, -52.37) * mm});
            skLineSegment(sketch, "E628", {"start": v(18.27, -52.37) * mm, "end": v(18.74, -52.37) * mm});
            skLineSegment(sketch, "E629", {"start": v(18.74, -52.37) * mm, "end": v(19.2, -52.37) * mm});
            skLineSegment(sketch, "E630", {"start": v(19.2, -52.37) * mm, "end": v(19.68, -52.37) * mm});
            skLineSegment(sketch, "E631", {"start": v(19.68, -52.37) * mm, "end": v(20.15, -52.37) * mm});
            skLineSegment(sketch, "E632", {"start": v(20.15, -52.37) * mm, "end": v(20.62, -52.37) * mm});
            skLineSegment(sketch, "E633", {"start": v(20.62, -52.37) * mm, "end": v(21.09, -52.37) * mm});
            skLineSegment(sketch, "E634", {"start": v(21.09, -52.37) * mm, "end": v(21.56, -52.37) * mm});
            skLineSegment(sketch, "E635", {"start": v(21.56, -52.37) * mm, "end": v(22.03, -52.37) * mm});
            skLineSegment(sketch, "E636", {"start": v(22.03, -52.37) * mm, "end": v(22.5, -52.37) * mm});
            skLineSegment(sketch, "E637", {"start": v(22.5, -52.37) * mm, "end": v(22.5, -49.94) * mm});
            skLineSegment(sketch, "E638", {"start": v(22.5, -49.94) * mm, "end": v(22.5, -47.51) * mm});
            skLineSegment(sketch, "E639", {"start": v(22.5, -47.51) * mm, "end": v(22.5, -45.09) * mm});
            skLineSegment(sketch, "E640", {"start": v(22.5, -45.09) * mm, "end": v(22.5, -42.66) * mm});
            skLineSegment(sketch, "E641", {"start": v(22.5, -42.66) * mm, "end": v(22.5, -40.23) * mm});
            skLineSegment(sketch, "E642", {"start": v(22.5, -40.23) * mm, "end": v(22.5, -37.8) * mm});
            skLineSegment(sketch, "E643", {"start": v(22.5, -37.8) * mm, "end": v(22.5, -35.38) * mm});
            skLineSegment(sketch, "E644", {"start": v(22.5, -35.38) * mm, "end": v(22.5, -32.96) * mm});
            skLineSegment(sketch, "E645", {"start": v(22.5, -32.96) * mm, "end": v(22.5, -30.53) * mm});
            skLineSegment(sketch, "E646", {"start": v(22.5, -30.53) * mm, "end": v(22.5, -28.1) * mm});
            skLineSegment(sketch, "E647", {"start": v(22.5, -28.1) * mm, "end": v(22.5, -25.68) * mm});
            skLineSegment(sketch, "E648", {"start": v(22.5, -25.68) * mm, "end": v(22.5, -23.25) * mm});
            skLineSegment(sketch, "E649", {"start": v(22.5, -23.25) * mm, "end": v(22.5, -20.82) * mm});
            skLineSegment(sketch, "E650", {"start": v(22.5, -20.82) * mm, "end": v(22.5, -18.4) * mm});
            skLineSegment(sketch, "E651", {"start": v(22.5, -18.4) * mm, "end": v(22.5, -15.97) * mm});
            skLineSegment(sketch, "E652", {"start": v(22.5, -15.97) * mm, "end": v(22.5, -13.54) * mm});
            skLineSegment(sketch, "E653", {"start": v(22.5, -13.54) * mm, "end": v(22.5, -11.12) * mm});
            skLineSegment(sketch, "E654", {"start": v(22.5, -11.12) * mm, "end": v(22.5, -8.7) * mm});
            skLineSegment(sketch, "E655", {"start": v(22.5, -8.7) * mm, "end": v(22.5, -6.27) * mm});
            skLineSegment(sketch, "E656", {"start": v(22.5, -6.27) * mm, "end": v(22.5, -3.84) * mm});
            skLineSegment(sketch, "E657", {"start": v(22.5, -3.84) * mm, "end": v(22.5, -1.41) * mm});
            skLineSegment(sketch, "E658", {"start": v(22.5, -1.41) * mm, "end": v(22.5, 1.01) * mm});
            skLineSegment(sketch, "E659", {"start": v(22.5, 1.01) * mm, "end": v(22.5, 3.44) * mm});
            skLineSegment(sketch, "E660", {"start": v(22.5, 3.44) * mm, "end": v(22.5, 5.87) * mm});
            skLineSegment(sketch, "E661", {"start": v(22.5, 5.87) * mm, "end": v(22.5, 8.3) * mm});
            skLineSegment(sketch, "E662", {"start": v(22.5, 8.3) * mm, "end": v(22.5, 10.72) * mm});
            skLineSegment(sketch, "E663", {"start": v(22.5, 10.72) * mm, "end": v(22.5, 13.14) * mm});
            skLineSegment(sketch, "E664", {"start": v(22.5, 13.14) * mm, "end": v(22.5, 15.57) * mm});
            skLineSegment(sketch, "E665", {"start": v(22.5, 15.57) * mm, "end": v(22.5, 18) * mm});
            skLineSegment(sketch, "E666", {"start": v(22.5, 18) * mm, "end": v(22.5, 20.42) * mm});
            skLineSegment(sketch, "E667", {"start": v(22.5, 20.42) * mm, "end": v(22.5, 22.85) * mm});
            skLineSegment(sketch, "E668", {"start": v(22.5, 22.85) * mm, "end": v(22.5, 25.28) * mm});
            skLineSegment(sketch, "E669", {"start": v(22.5, 25.28) * mm, "end": v(22.48, 26.3) * mm});
            skLineSegment(sketch, "E670", {"start": v(22.48, 26.3) * mm, "end": v(22.4, 27.33) * mm});
            skLineSegment(sketch, "E671", {"start": v(22.4, 27.33) * mm, "end": v(22.3, 28.34) * mm});
            skLineSegment(sketch, "E672", {"start": v(22.3, 28.34) * mm, "end": v(22.14, 29.33) * mm});
            skLineSegment(sketch, "E673", {"start": v(22.14, 29.33) * mm, "end": v(21.94, 30.3) * mm});
            skLineSegment(sketch, "E674", {"start": v(21.94, 30.3) * mm, "end": v(21.7, 31.27) * mm});
            skLineSegment(sketch, "E675", {"start": v(21.7, 31.27) * mm, "end": v(21.4, 32.21) * mm});
            skLineSegment(sketch, "E676", {"start": v(21.4, 32.21) * mm, "end": v(21.09, 33.14) * mm});
            skLineSegment(sketch, "E677", {"start": v(21.09, 33.14) * mm, "end": v(20.72, 34.05) * mm});
            skLineSegment(sketch, "E678", {"start": v(20.72, 34.05) * mm, "end": v(20.32, 34.94) * mm});
            skLineSegment(sketch, "E679", {"start": v(20.32, 34.94) * mm, "end": v(19.89, 35.8) * mm});
            skLineSegment(sketch, "E680", {"start": v(19.89, 35.8) * mm, "end": v(19.42, 36.65) * mm});
            skLineSegment(sketch, "E681", {"start": v(19.42, 36.65) * mm, "end": v(18.9, 37.47) * mm});
            skLineSegment(sketch, "E682", {"start": v(18.9, 37.47) * mm, "end": v(18.37, 38.27) * mm});
            skLineSegment(sketch, "E683", {"start": v(18.37, 38.27) * mm, "end": v(17.8, 39.05) * mm});
            skLineSegment(sketch, "E684", {"start": v(17.8, 39.05) * mm, "end": v(17.19, 39.8) * mm});
            skLineSegment(sketch, "E685", {"start": v(17.19, 39.8) * mm, "end": v(16.55, 40.52) * mm});
            skLineSegment(sketch, "E686", {"start": v(16.55, 40.52) * mm, "end": v(15.88, 41.2) * mm});
            skLineSegment(sketch, "E687", {"start": v(15.88, 41.2) * mm, "end": v(15.19, 41.87) * mm});
            skLineSegment(sketch, "E688", {"start": v(15.19, 41.87) * mm, "end": v(14.46, 42.5) * mm});
            skLineSegment(sketch, "E689", {"start": v(14.46, 42.5) * mm, "end": v(13.71, 43.1) * mm});
            skLineSegment(sketch, "E690", {"start": v(13.71, 43.1) * mm, "end": v(12.94, 43.68) * mm});
            skLineSegment(sketch, "E691", {"start": v(12.94, 43.68) * mm, "end": v(12.14, 44.22) * mm});
            skLineSegment(sketch, "E692", {"start": v(12.14, 44.22) * mm, "end": v(11.31, 44.72) * mm});
            skLineSegment(sketch, "E693", {"start": v(11.31, 44.72) * mm, "end": v(10.46, 45.2) * mm});
            skLineSegment(sketch, "E694", {"start": v(10.46, 45.2) * mm, "end": v(9.6, 45.63) * mm});
            skLineSegment(sketch, "E695", {"start": v(9.6, 45.63) * mm, "end": v(8.7, 46.02) * mm});
            skLineSegment(sketch, "E696", {"start": v(8.7, 46.02) * mm, "end": v(7.8, 46.38) * mm});
            skLineSegment(sketch, "E697", {"start": v(6.87, 46.7) * mm, "end": v(5.92, 46.98) * mm});
            skLineSegment(sketch, "E698", {"start": v(5.92, 46.98) * mm, "end": v(4.95, 47.22) * mm});
            skLineSegment(sketch, "E699", {"start": v(4.95, 47.22) * mm, "end": v(3.98, 47.42) * mm});
            skLineSegment(sketch, "E700", {"start": v(0, 52.37) * mm, "end": v(0, -31.83) * mm});
            skPoint(sketch, "E701.orphan", {"position": v(0, 59.24) * mm});
            skSolve(sketch);
        }
        {
            var Q0;
            Q0 = qSketchRegion(id + "F0", true);
            var Q1;
            Q1=sQuery(id+"F0.wireOp",EDGE,"E700");
            revolve(context, id + "F1", {"entities" : qUnion([Q0]), "axis" : qUnion([Q1]), "revolveType" : RevolveType.FULL});
        }
    });
